# Revit family: Вытяжная секция рекуператора с промежуточным теплоносителем AIRNED-M G2
name_source: partatom
category: Оборудование
revit_build: Autodesk Revit 2017 (Build: 20160225_1515(x64)
units: mm (PartAtom-declared; Revit-internal decimal feet)

## family parameters
Всегда вертикально = Да
На основе рабочей плоскости = Нет
Общий = Нет
При загрузке вырезать с полостями = Нет
Размер круглого соединителя = Использовать диаметр
Тип детали = Нормальный
Точка расчета площади = Нет

## types (8) — shared parameters
h = 130 мм
Д = 1100 мм
Д1 = 1080 мм
Единица измерения = шт.
Завод изготовитель = NED
К = 275 мм
Ключевая пометка = Вентиляция
Материал = Сталь серая
Наименование и тех.хар-ка = Вытяжная секция рекуператора с промежуточным теплоносителем
Раздел = ОВ
высота ножек = 120 мм

## per-type parameters (varying)
| type | А | А1 | Б | Б1 | Высота | Г | Д патрубков | Заправочный объем, л | И | И1 | Размер В | Резьбовое соединение, дюймы | Середина | Ширина |
| AIRNED-M 6 G2 | 1100 мм | 1080 мм | 1100 мм | 1080 мм | 1025 мм | 212 мм | 64 мм | 27.2 м³ | 135 мм | 125 мм | 710 мм | G2 1/2'' | 670 мм | 1025 мм |
| AIRNED-M 7 G2 | 1100 мм | 1080 мм | 1320 мм | 1300 мм | 1245 мм | 212 мм | 76 мм | 38.8 м³ | 115 мм | 105 мм | 944 мм | G3'' | 780 мм | 1025 мм |
| AIRNED-M 8 G2 | 1320 мм | 1300 мм | 1320 мм | 1300 мм | 1245 мм | 212 мм | 76 мм | 45.2 м³ | 115 мм | 105 мм | 944 мм | G3'' | 780 мм | 1245 мм |
| AIRNED-M 20 G2 | 1660 мм | 1640 мм | 1660 мм | 1640 мм | 1585 мм | 212 мм | 51 мм | 84.3 м³ | 115 мм | 105 мм | 1294 мм | G3'' | 950 мм | 1585 мм |
| AIRNED-M 25 G2 | 2045 мм | 2025 мм | 2045 мм | 2025 мм | 1970 мм | 182 мм | 102 мм | 48.6 м³ | 115 мм | 105 мм | 1653 мм | G4'' | 1143 мм | 1970 мм |
| AIRNED-M 30 G2 | 2485 мм | 2465 мм | 2045 мм | 2025 мм | 1970 мм | 182 мм | 64 мм | 149.3 м³ | 115 мм | 105 мм | 1653 мм | G4'' | 1143 мм | 2410 мм |
| AIRNED-M 35 G2 | 2485 мм | 2465 мм | 2485 мм | 2465 мм | 2410 мм | 182 мм | 102 мм | 188.1 м³ | 115 мм | 105 мм | 2095 мм | G4'' | 1363 мм | 2410 мм |
| AIRNED-M 12 G2 | 1435 мм | 1415 мм | 1435 мм | 1415 мм | 1360 мм | 212 мм | 76 мм | 54.7 м³ | 115 мм | 105 мм | 1069 мм | G3'' | 838 мм | 1360 мм |

note: column(s) folded — value = type name in every type: Тип, марка, обозначение
